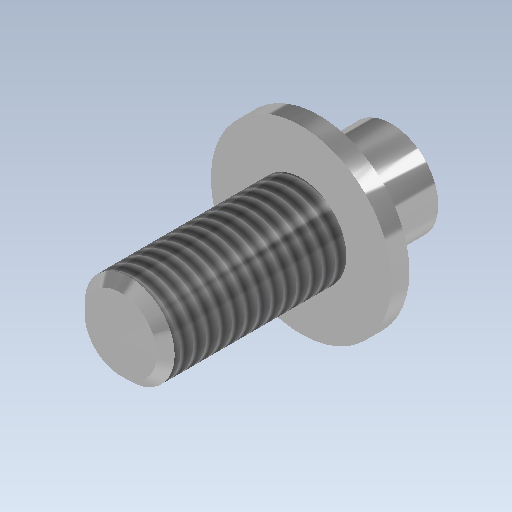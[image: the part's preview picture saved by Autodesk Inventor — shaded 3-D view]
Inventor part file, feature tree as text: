
AUTODESK INVENTOR PART (.ipt)
format: ipt  version: 2020 (Build 240168000, 168)  size: 193,024 bytes
history: native  units: mm (DEFAULTED — no unit token found)
features: extrude x3, sketch x3, chamfer x1, thread x1
ambient origin geometry x8: Origin, YZ Plane, XZ Plane, XY Plane, X Axis, Y Axis, Z Axis, Center Point
bodies: Solid1 (feature_tree)
feature tree (8):
  extrude  "Extrusion1"  Depth=1.27mm TaperAngle=0.0deg
  extrude  "Extrusion2"  Depth=12.7mm TaperAngle=0.0deg
  chamfer  "Chamfer1"  Distance=0.635mm
  thread  "Thread1"  [1 undecoded]
  extrude  "Extrusion3"  Depth=5.08mm TaperAngle=0.0deg
  sketch  "Sketch1"  dims[d0=12.7mm d1=1.27mm d2=0.0mm]
  sketch  "Sketch2"  dims[d3=6.35mm d4=12.7mm d5=0.0mm d6=0.635mm d7=0.635mm d8=25.4mm d9=0.0mm]
  sketch  "Sketch3"  dims[d10=6.604mm d11=5.08mm d12=0.0mm d13=45.0deg]
note: 1 required parameter value undecoded (feature->parameter linkage not recoverable at this tier; creation-order binding heuristic only, values carry confidence <= 0.55)
